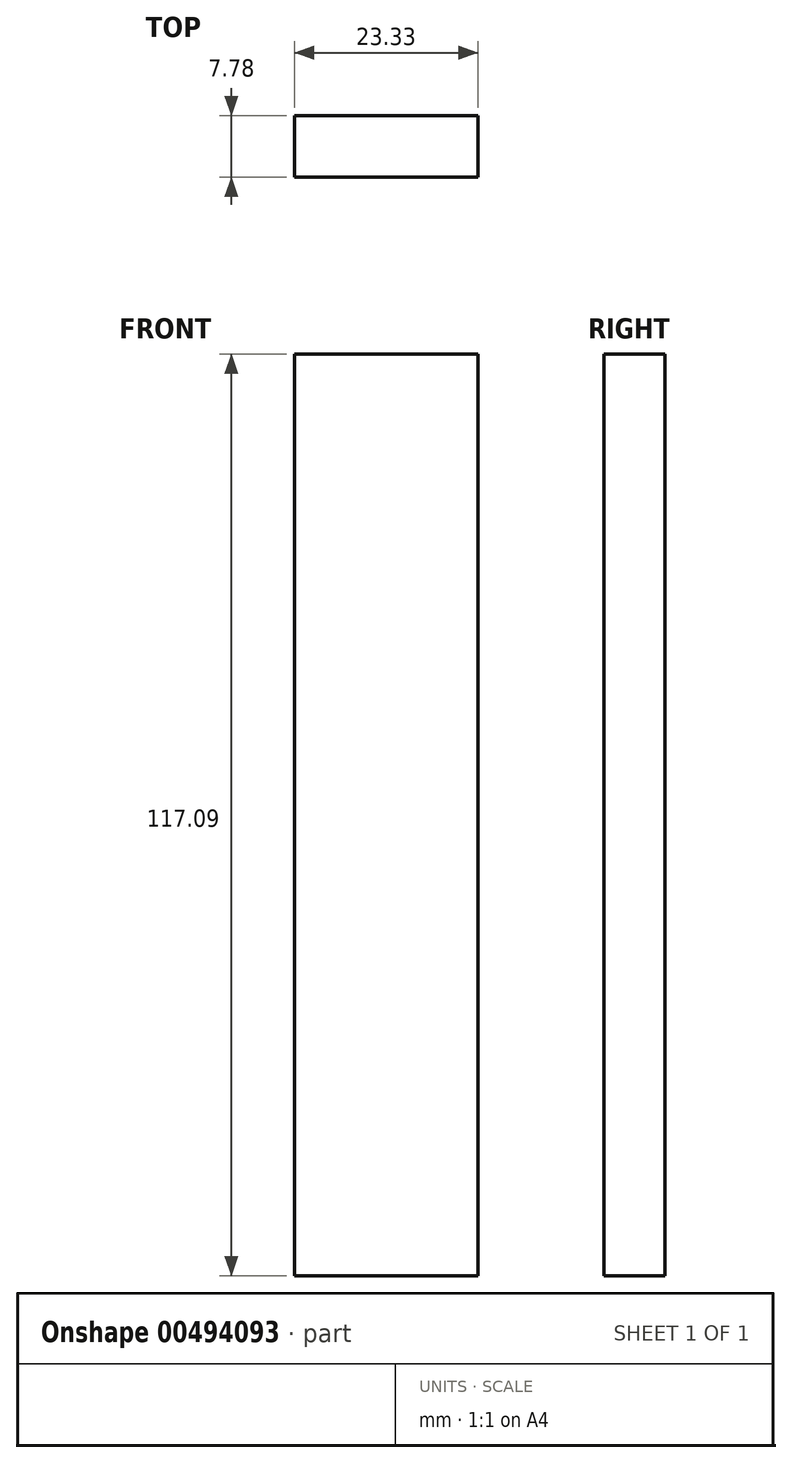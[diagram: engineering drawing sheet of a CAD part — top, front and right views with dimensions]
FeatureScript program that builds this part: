
annotation { "Feature Type Name" : "Feature", "Feature Type Description" : "" }
export const myFeature = defineFeature(function(context is Context, id is Id, definition is map)
    precondition{}
    {
        {
            var Q0;
            Q0=qCreatedBy(makeId("Front.planeOp"),FACE);
            var sketch = newSketch(context, id + "F0", { "sketchPlane" : qUnion([Q0])});
            skLineSegment(sketch, "E0.bottom", {"start": v(-16.03, 77.3) * mm, "end": v(7.3, 77.3) * mm});
            skLineSegment(sketch, "E0.top", {"start": v(-16.03, -39.79) * mm, "end": v(7.3, -39.79) * mm});
            skLineSegment(sketch, "E0.left", {"start": v(-16.03, 77.3) * mm, "end": v(-16.03, -39.79) * mm});
            skLineSegment(sketch, "E0.right", {"start": v(7.3, 77.3) * mm, "end": v(7.3, -39.79) * mm});
            skSolve(sketch);
        }
        {
            var Q0;
            Q0=makeQuery(id+"F0.imprint","IMPRINT",FACE,{"disambiguationData":[TD([[makeQuery(id+"F0.imprint","IMPRINT",EDGE,{"derivedFrom":sQuery(id+"F0.wireOp",EDGE,"E0.bottom")}),-1.0]])]});
            extrude(context, id + "F1", {"entities" : qUnion([Q0]), "depth" : 7.78 * mm});
        }
    });
